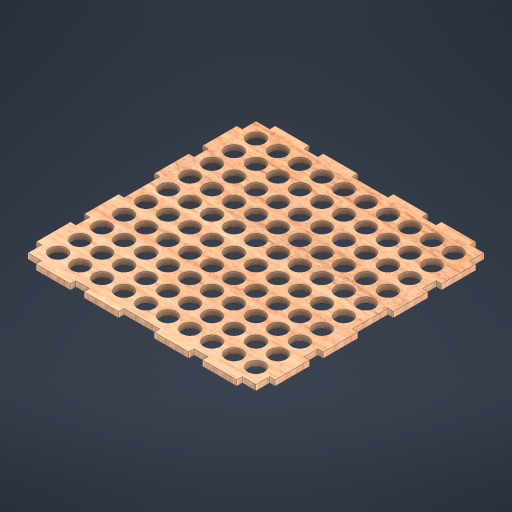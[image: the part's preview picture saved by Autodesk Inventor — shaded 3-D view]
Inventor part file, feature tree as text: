
AUTODESK INVENTOR PART (.ipt)
format: ipt  version: 2024.1 (Build 281209000, 209)  size: 616,960 bytes
history: native  units: mm
features: extrude x1, sketch x1
ambient origin geometry x8: Origin, YZ Plane, XZ Plane, XY Plane, X Axis, Y Axis, Z Axis, Center Point
bodies: Solid1 (feature_tree)
feature tree (2):
  extrude  "Extrusion1"  Depth=100.0mm
  sketch  "Sketch1"  dims[d0=12.0mm d1=100.0mm d3=16.0mm d4=100.0mm d6=16.0mm d9=5.0mm d10=5.0mm d11=4.0mm d12=4.0mm d13=10.0mm d14=10.0mm d15=25.0mm d16=4.0mm d17=25.0mm d18=10.0mm d19=25.0mm d20=10.0mm d21=25.0mm d22=4.0mm d23=40.0mm d25=360.0deg d27=4.0mm d28=0.0mm]
